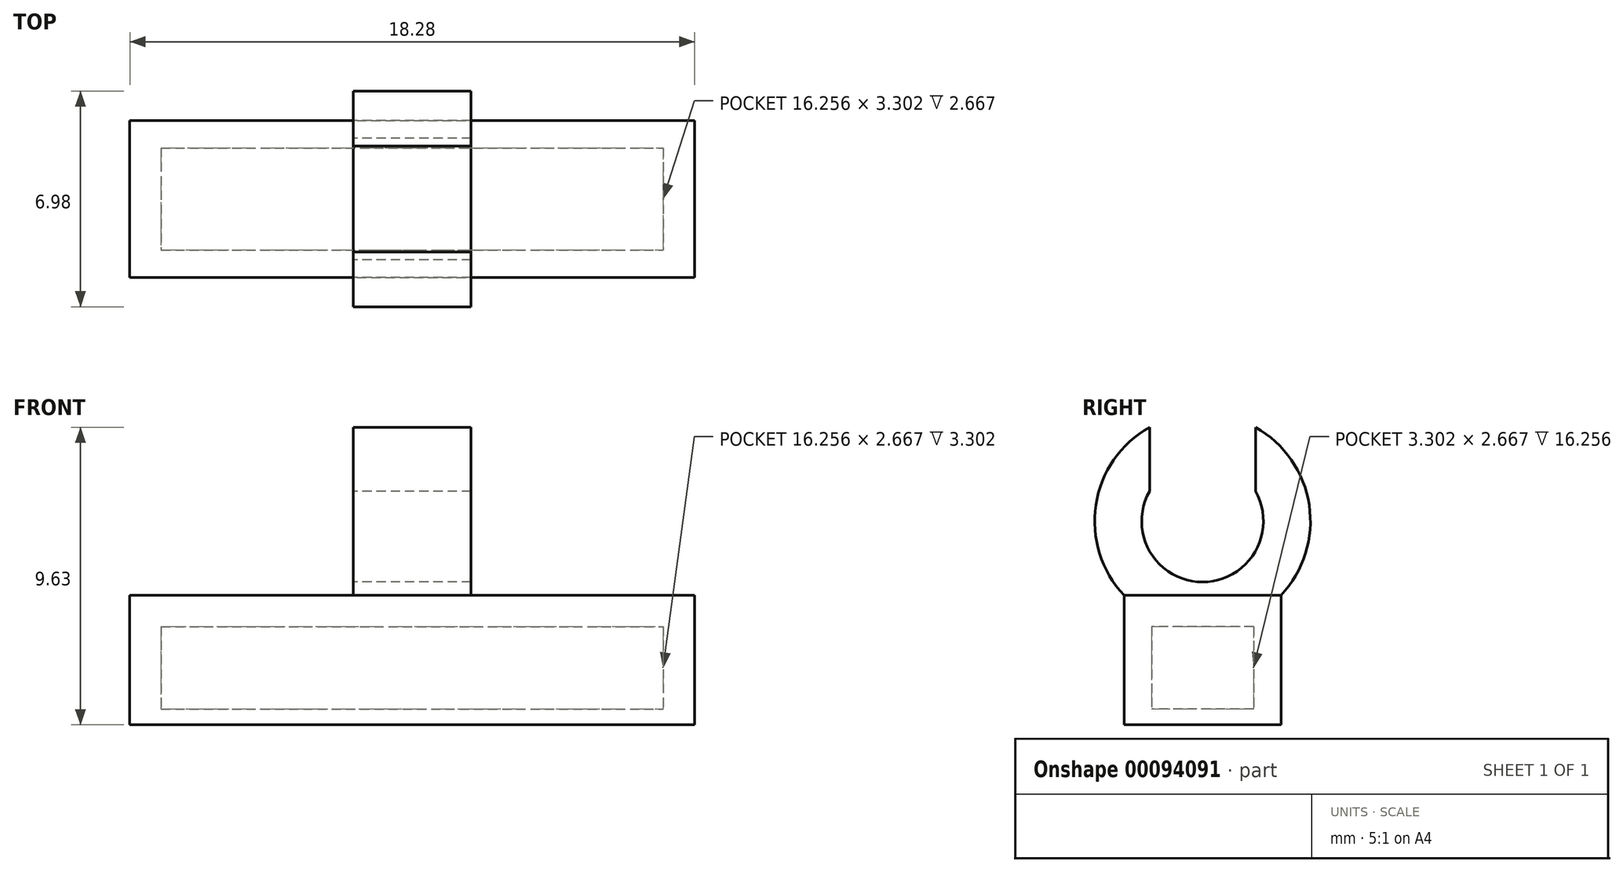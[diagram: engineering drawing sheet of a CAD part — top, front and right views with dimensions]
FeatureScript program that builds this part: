
annotation { "Feature Type Name" : "Feature", "Feature Type Description" : "" }
export const myFeature = defineFeature(function(context is Context, id is Id, definition is map)
    precondition{}
    {
        {
            var Q0;
            Q0=qCreatedBy(makeId("Top.planeOp"),FACE);
            var sketch = newSketch(context, id + "F0", { "sketchPlane" : qUnion([Q0])});
            skLineSegment(sketch, "E0.bottom", {"start": v(-9.14, 5.08) * mm, "end": v(9.14, 5.08) * mm});
            skLineSegment(sketch, "E0.top", {"start": v(-9.14, 0) * mm, "end": v(9.14, 0) * mm});
            skLineSegment(sketch, "E0.left", {"start": v(-9.14, 5.08) * mm, "end": v(-9.14, 0) * mm});
            skLineSegment(sketch, "E0.right", {"start": v(9.14, 5.08) * mm, "end": v(9.14, 0) * mm});
            skPoint(sketch, "E1", {"position": v(0, 0) * mm});
            skLineSegment(sketch, "E2", {"start": v(0, 0) * mm, "end": v(0, 5.08) * mm, "construction": true});
            skLineSegment(sketch, "E3.bottom", {"start": v(-8.13, 4.2) * mm, "end": v(8.13, 4.2) * mm});
            skLineSegment(sketch, "E3.top", {"start": v(-8.13, 0.89) * mm, "end": v(8.13, 0.89) * mm});
            skLineSegment(sketch, "E3.left", {"start": v(-8.13, 4.2) * mm, "end": v(-8.13, 0.89) * mm});
            skLineSegment(sketch, "E3.right", {"start": v(8.13, 4.2) * mm, "end": v(8.13, 0.89) * mm});
            skPoint(sketch, "E4", {"position": v(0, 0.89) * mm});
            skPoint(sketch, "E5", {"position": v(0, 2.54) * mm});
            skLineSegment(sketch, "E6", {"start": v(-8.13, 2.54) * mm, "end": v(8.13, 2.54) * mm, "construction": true});
            skSolve(sketch);
        }
        {
            var Q0;
            Q0=makeQuery(id+"F0.imprint","IMPRINT",FACE,{"disambiguationData":[TD([[makeQuery(id+"F0.imprint","IMPRINT",EDGE,{"derivedFrom":sQuery(id+"F0.wireOp",EDGE,"E0.bottom")}),-1.0]])]});
            extrude(context, id + "F1", {"entities" : qUnion([Q0]), "depth" : 3.17 * mm, "offsetDistance" : 25.4 * mm});
        }
        {
            var Q0;
            Q0=makeQuery(id+"F1.opExtrude","CAP_FACE",FACE,{"disambiguationData":[OSD([sQuery(id+"F0.wireOp",EDGE,"E0.bottom"),sQuery(id+"F0.wireOp",EDGE,"E0.top"),sQuery(id+"F0.wireOp",EDGE,"E0.left"),sQuery(id+"F0.wireOp",EDGE,"E0.right"),sQuery(id+"F0.wireOp",EDGE,"E3.bottom"),sQuery(id+"F0.wireOp",EDGE,"E3.top"),sQuery(id+"F0.wireOp",EDGE,"E3.left"),sQuery(id+"F0.wireOp",EDGE,"E3.right")])],"isStart":true});
            var sketch = newSketch(context, id + "F2", { "sketchPlane" : qUnion([Q0])});
            skLineSegment(sketch, "E7.0", {"start": v(-9.14, -5.08) * mm, "end": v(9.14, -5.08) * mm});
            skLineSegment(sketch, "E8.0", {"start": v(9.14, -5.08) * mm, "end": v(9.14, 0) * mm});
            skLineSegment(sketch, "E9.0", {"start": v(-9.14, 0) * mm, "end": v(9.14, 0) * mm});
            skLineSegment(sketch, "E10.0", {"start": v(-9.14, -5.08) * mm, "end": v(-9.14, 0) * mm});
            skSolve(sketch);
        }
        {
            var Q0;
            Q0=makeQuery(id+"F2.imprint","IMPRINT",FACE,{"disambiguationData":[TD([[makeQuery(id+"F2.imprint","IMPRINT",EDGE,{"derivedFrom":makeQuery(id+"F1.opExtrude","CAP_EDGE",EDGE,{"disambiguationData":[OSD([sQuery(id+"F0.wireOp",EDGE,"E3.bottom")])],"isStart":true})}),1.0]])]});
            extrude(context, id + "F3", {"entities" : qUnion([Q0]), "operationType" : NewBodyOperationType.ADD, "oppositeDirection" : true, "depth" : 0.5 * mm, "offsetDistance" : 25.4 * mm});
        }
        {
            var Q0;
            Q0=makeQuery(id+"F1.opExtrude","CAP_FACE",FACE,{"disambiguationData":[OSD([sQuery(id+"F0.wireOp",EDGE,"E0.bottom"),sQuery(id+"F0.wireOp",EDGE,"E0.top"),sQuery(id+"F0.wireOp",EDGE,"E0.left"),sQuery(id+"F0.wireOp",EDGE,"E0.right"),sQuery(id+"F0.wireOp",EDGE,"E3.bottom"),sQuery(id+"F0.wireOp",EDGE,"E3.top"),sQuery(id+"F0.wireOp",EDGE,"E3.left"),sQuery(id+"F0.wireOp",EDGE,"E3.right")])],"isStart":false});
            var sketch = newSketch(context, id + "F4", { "sketchPlane" : qUnion([Q0])});
            skLineSegment(sketch, "E11.0", {"start": v(-9.14, 5.08) * mm, "end": v(9.14, 5.08) * mm});
            skLineSegment(sketch, "E12.0", {"start": v(-9.14, 5.08) * mm, "end": v(-9.14, 0) * mm});
            skLineSegment(sketch, "E13.0", {"start": v(-9.14, 0) * mm, "end": v(9.14, 0) * mm});
            skLineSegment(sketch, "E14.0", {"start": v(9.14, 5.08) * mm, "end": v(9.14, 0) * mm});
            skSolve(sketch);
        }
        {
            var Q0;
            Q0=makeQuery(id+"F4.imprint","IMPRINT",FACE,{"disambiguationData":[TD([[makeQuery(id+"F4.imprint","IMPRINT",EDGE,{"derivedFrom":makeQuery(id+"F1.opExtrude","CAP_EDGE",EDGE,{"disambiguationData":[OSD([sQuery(id+"F0.wireOp",EDGE,"E3.bottom")])],"isStart":false})}),-1.0]])]});
            var Q1;
            Q1=makeQuery(id+"F4.imprint","IMPRINT",FACE,{"disambiguationData":[TD([[makeQuery(id+"F4.imprint","IMPRINT",EDGE,{"derivedFrom":sQuery(id+"F4.wireOp",EDGE,"E11.0")}),-1.0]])]});
            extrude(context, id + "F5", {"entities" : qUnion([Q0, Q1]), "operationType" : NewBodyOperationType.ADD, "depth" : 1.02 * mm, "offsetDistance" : 25.4 * mm});
        }
        {
            var Q0;
            Q0=qCreatedBy(makeId("Right.planeOp"),FACE);
            var sketch = newSketch(context, id + "F6", { "sketchPlane" : qUnion([Q0])});
            skLineSegment(sketch, "E15", {"start": v(5.08, 4.2) * mm, "end": v(0, 4.2) * mm});
            skLineSegment(sketch, "E16", {"start": v(0, 0) * mm, "end": v(0, 4.2) * mm});
            skLineSegment(sketch, "E17", {"start": v(5.08, 0) * mm, "end": v(5.08, 4.2) * mm});
            skLineSegment(sketch, "E18", {"start": v(2.54, 4.2) * mm, "end": v(2.54, 11.74) * mm, "construction": true});
            skCircle(sketch, "E19", {"center": v(2.54, 6.59) * mm, "radius": 3.5 * mm});
            skCircle(sketch, "E20", {"center": v(2.54, 6.59) * mm, "radius": 1.97 * mm});
            skLineSegment(sketch, "E21.bottom", {"start": v(0.83, 7.56) * mm, "end": v(4.25, 7.56) * mm});
            skLineSegment(sketch, "E21.top", {"start": v(0.83, 9.63) * mm, "end": v(4.25, 9.63) * mm});
            skLineSegment(sketch, "E21.left", {"start": v(0.83, 7.56) * mm, "end": v(0.83, 9.63) * mm});
            skLineSegment(sketch, "E21.right", {"start": v(4.25, 7.56) * mm, "end": v(4.25, 9.63) * mm});
            skSolve(sketch);
        }
        {
            var Q0;
            {var subQ5=sQuery(id+"F6.wireOp",EDGE,"E15");Q0=makeQuery(id+"F6.imprint","IMPRINT",FACE,{"disambiguationData":[TD([[makeQuery(id+"F6.imprint","IMPRINT",EDGE,{"derivedFrom":subQ5}),-1.0]])]});}
            extrude(context, id + "F7", {"entities" : qUnion([Q0]), "operationType" : NewBodyOperationType.ADD, "depth" : 3.8 * mm, "offsetDistance" : 25.4 * mm, "symmetric" : true});
        }
    });
